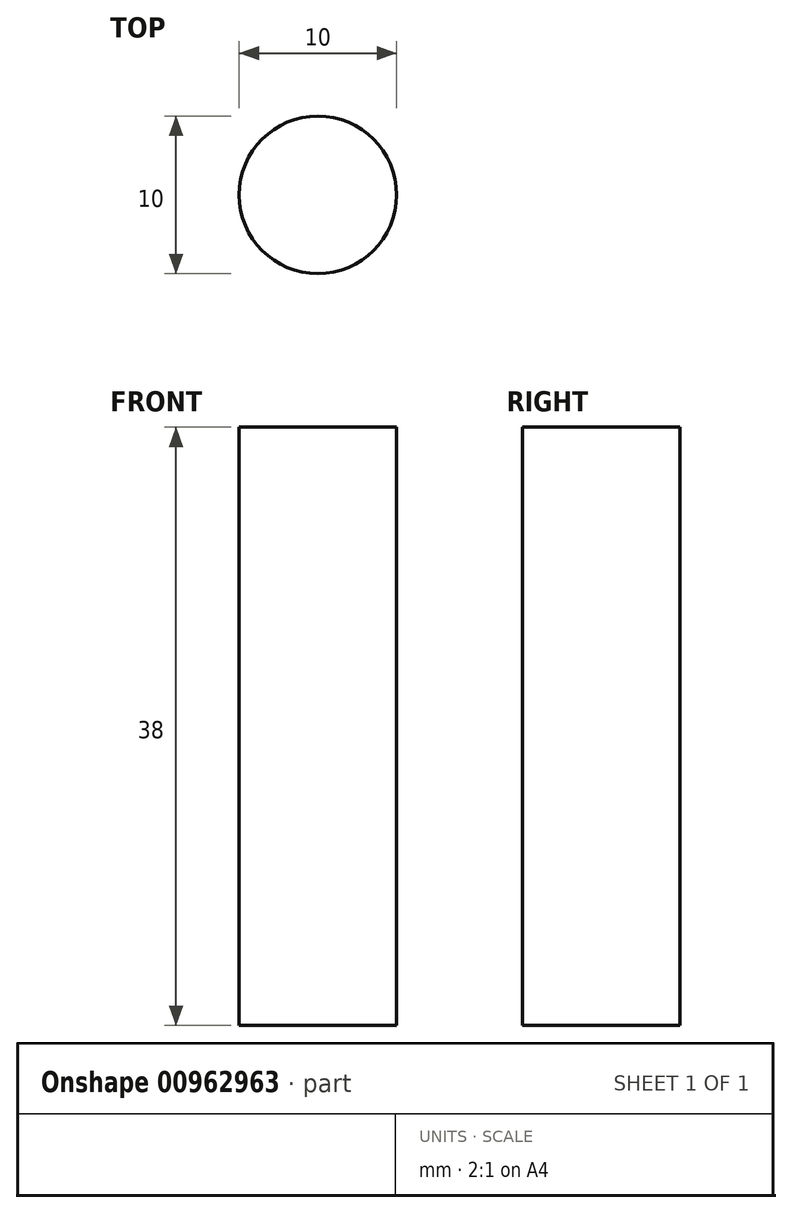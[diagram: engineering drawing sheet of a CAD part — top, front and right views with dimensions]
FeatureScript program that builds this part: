
annotation { "Feature Type Name" : "Feature", "Feature Type Description" : "" }
export const myFeature = defineFeature(function(context is Context, id is Id, definition is map)
    precondition{}
    {
        {
            var Q0;
            Q0=qCreatedBy(makeId("Top.planeOp"),FACE);
            var sketch = newSketch(context, id + "F0", { "sketchPlane" : qUnion([Q0])});
            skCircle(sketch, "E0", {"center": v(0, 0) * mm, "radius": 5 * mm});
            skSolve(sketch);
        }
        {
            var Q0;
            Q0 = qSketchRegion(id + "F0", true);
            extrude(context, id + "F1", {"entities" : qUnion([Q0]), "depth" : 38 * mm, "offsetDistance" : 25 * mm, "symmetric" : true});
        }
    });
